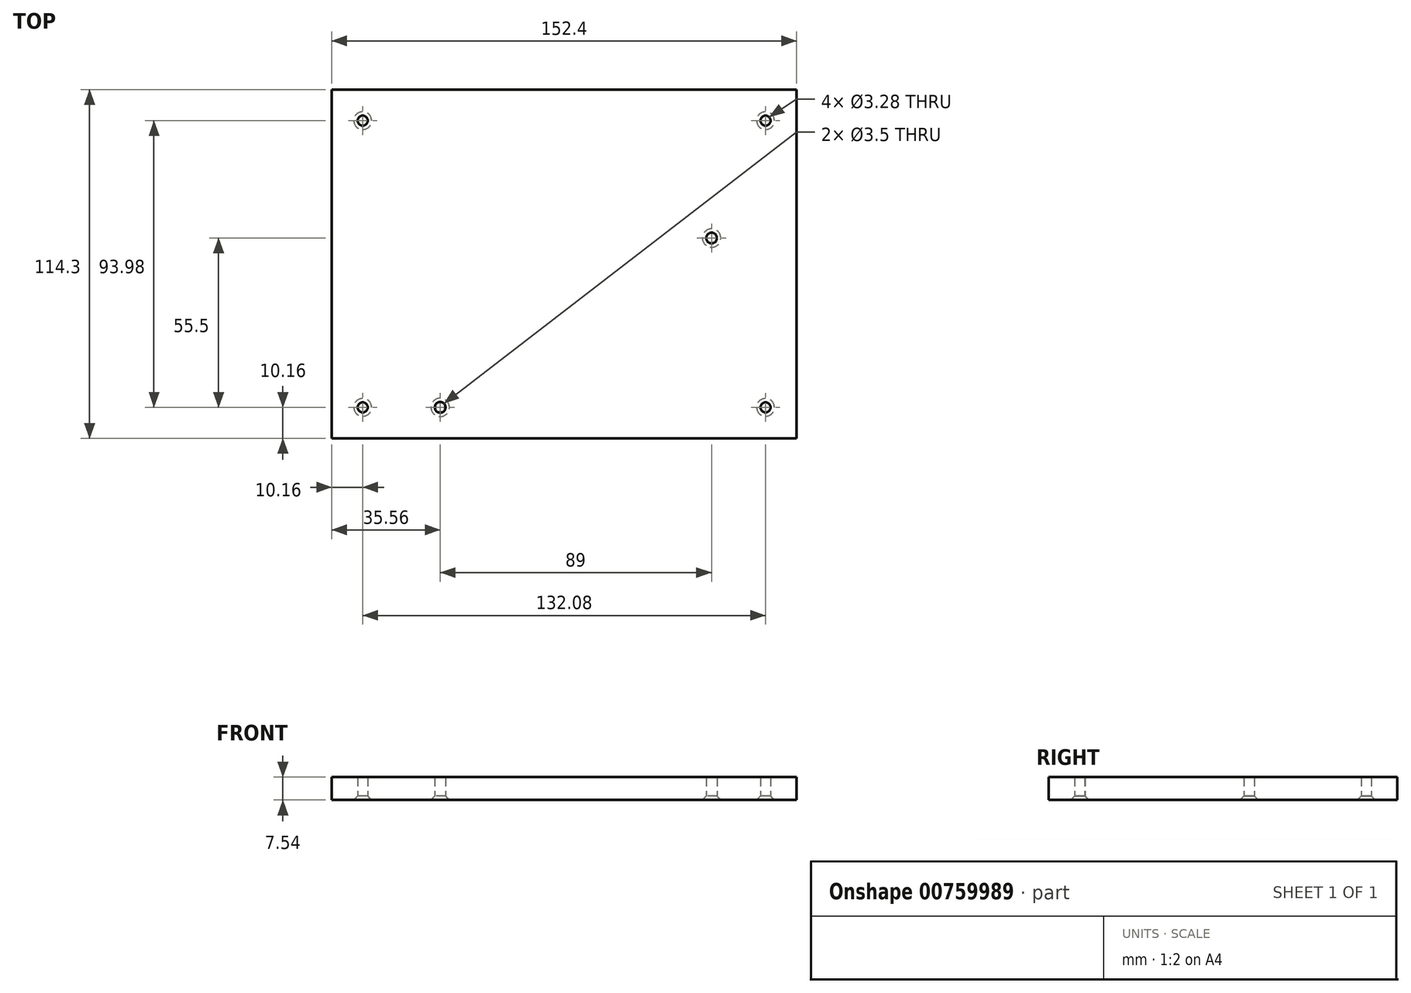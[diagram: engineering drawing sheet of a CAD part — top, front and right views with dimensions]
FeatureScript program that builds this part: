
annotation { "Feature Type Name" : "Feature", "Feature Type Description" : "" }
export const myFeature = defineFeature(function(context is Context, id is Id, definition is map)
    precondition{}
    {
        {
            var Q0;
            Q0=qCreatedBy(makeId("Top.planeOp"),FACE);
            var sketch = newSketch(context, id + "F0", { "sketchPlane" : qUnion([Q0])});
            skLineSegment(sketch, "E0", {"start": v(0, 0) * mm, "end": v(0, 47) * mm, "construction": true});
            skLineSegment(sketch, "E1", {"start": v(0, 46.99) * mm, "end": v(-66.04, 46.99) * mm, "construction": true});
            skLineSegment(sketch, "E2", {"start": v(-66.04, 47) * mm, "end": v(-66.04, -46.99) * mm, "construction": true});
            skLineSegment(sketch, "E3", {"start": v(-66.04, -47) * mm, "end": v(66.04, -46.99) * mm, "construction": true});
            skLineSegment(sketch, "E4", {"start": v(66.04, -46.99) * mm, "end": v(66.04, 47) * mm, "construction": true});
            skLineSegment(sketch, "E5", {"start": v(66.04, 47) * mm, "end": v(0, 46.99) * mm, "construction": true});
            skLineSegment(sketch, "E6", {"start": v(0, 0) * mm, "end": v(0, -47) * mm, "construction": true});
            skCircle(sketch, "E7", {"center": v(-66.04, 46.99) * mm, "radius": 1.64 * mm});
            skCircle(sketch, "E8", {"center": v(66.04, 47) * mm, "radius": 1.64 * mm});
            skCircle(sketch, "E9", {"center": v(66.04, -46.99) * mm, "radius": 1.64 * mm});
            skCircle(sketch, "E10", {"center": v(-66.04, -46.99) * mm, "radius": 1.64 * mm});
            skCircle(sketch, "E11", {"center": v(-40.64, -47) * mm, "radius": 1.75 * mm});
            skCircle(sketch, "E12", {"center": v(48.36, 8.5) * mm, "radius": 1.75 * mm});
            skLineSegment(sketch, "E13", {"start": v(48.36, 8.5) * mm, "end": v(48.36, -47) * mm, "construction": true});
            skLineSegment(sketch, "E14.bottom", {"start": v(-76.2, 57.15) * mm, "end": v(76.2, 57.15) * mm});
            skLineSegment(sketch, "E14.top", {"start": v(-76.2, -57.15) * mm, "end": v(76.2, -57.15) * mm});
            skLineSegment(sketch, "E14.left", {"start": v(-76.2, 57.15) * mm, "end": v(-76.2, -57.15) * mm});
            skLineSegment(sketch, "E14.right", {"start": v(76.2, 57.15) * mm, "end": v(76.2, -57.15) * mm});
            skLineSegment(sketch, "E15", {"start": v(-66.04, 46.99) * mm, "end": v(-66.04, 57.15) * mm, "construction": true});
            skLineSegment(sketch, "E16", {"start": v(-66.04, 46.99) * mm, "end": v(-76.2, 46.99) * mm, "construction": true});
            skLineSegment(sketch, "E17", {"start": v(66.04, 47) * mm, "end": v(76.2, 47) * mm, "construction": true});
            skLineSegment(sketch, "E18", {"start": v(66.04, 47) * mm, "end": v(66.04, 57.15) * mm, "construction": true});
            skSolve(sketch);
        }
        {
            var Q0;
            Q0=makeQuery(id+"F0.imprint","IMPRINT",FACE,{"disambiguationData":[TD([[makeQuery(id+"F0.imprint","IMPRINT",EDGE,{"derivedFrom":sQuery(id+"F0.wireOp",EDGE,"E7")}),-1.0]])]});
            extrude(context, id + "F1", {"entities" : qUnion([Q0]), "depth" : 7.54 * mm, "offsetDistance" : 25.4 * mm});
        }
        {
            var Q0;
            Q0=makeQuery(id+"F1.opExtrude","CAP_EDGE",EDGE,{"disambiguationData":[OSD([sQuery(id+"F0.wireOp",EDGE,"E10")])],"isStart":true});
            var Q1;
            Q1=makeQuery(id+"F1.opExtrude","CAP_EDGE",EDGE,{"disambiguationData":[OSD([sQuery(id+"F0.wireOp",EDGE,"E11")])],"isStart":true});
            var Q2;
            Q2=makeQuery(id+"F1.opExtrude","CAP_EDGE",EDGE,{"disambiguationData":[OSD([sQuery(id+"F0.wireOp",EDGE,"E12")])],"isStart":true});
            var Q3;
            Q3=makeQuery(id+"F1.opExtrude","CAP_EDGE",EDGE,{"disambiguationData":[OSD([sQuery(id+"F0.wireOp",EDGE,"E8")])],"isStart":true});
            var Q4;
            Q4=makeQuery(id+"F1.opExtrude","CAP_EDGE",EDGE,{"disambiguationData":[OSD([sQuery(id+"F0.wireOp",EDGE,"E9")])],"isStart":true});
            var Q5;
            Q5=makeQuery(id+"F1.opExtrude","CAP_EDGE",EDGE,{"disambiguationData":[OSD([sQuery(id+"F0.wireOp",EDGE,"E7")])],"isStart":true});
            chamfer(context, id + "F2", {"entities" : qUnion([Q0, Q1, Q2, Q3, Q4, Q5]), "width" : 1.27 * mm, "tangentPropagation" : true});
        }
    });
